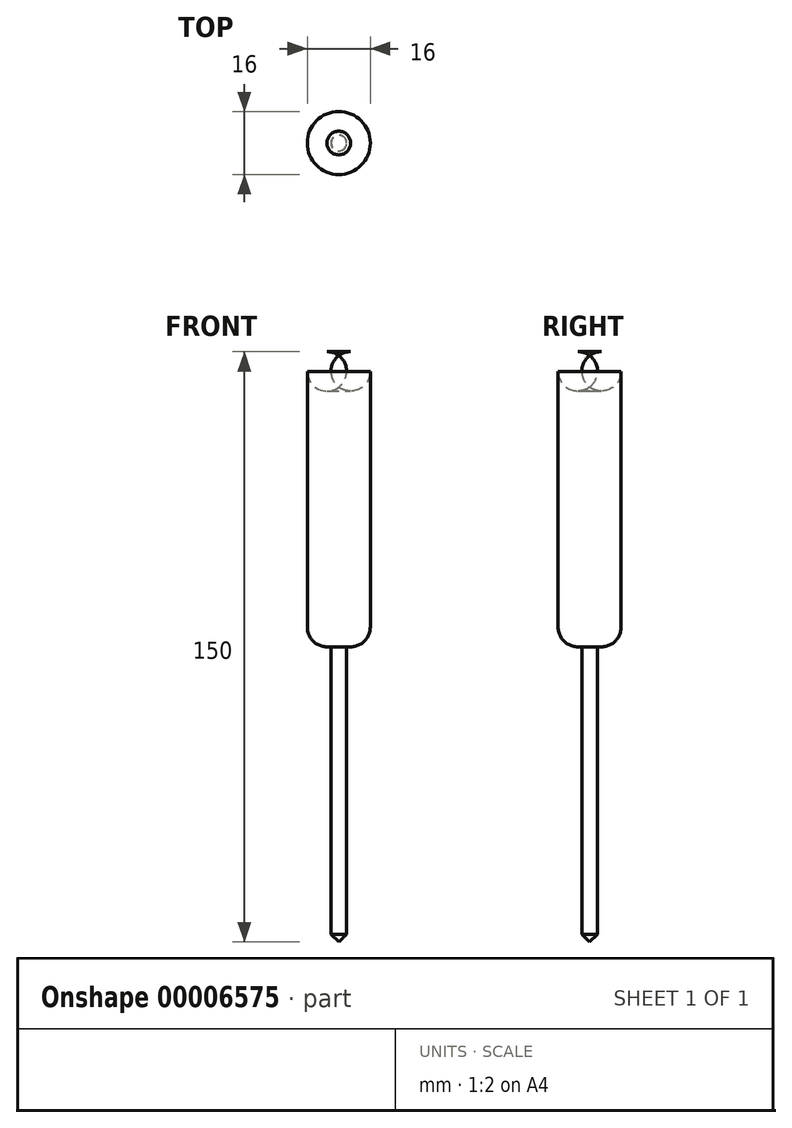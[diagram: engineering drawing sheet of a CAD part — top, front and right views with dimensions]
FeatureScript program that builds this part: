
annotation { "Feature Type Name" : "Feature", "Feature Type Description" : "" }
export const myFeature = defineFeature(function(context is Context, id is Id, definition is map)
    precondition{}
    {
        {
            var Q0;
            Q0=qCreatedBy(makeId("Front.planeOp"),FACE);
            var sketch = newSketch(context, id + "F0", { "sketchPlane" : qUnion([Q0])});
            skLineSegment(sketch, "E0.bottom", {"start": v(-8, 75) * mm, "end": v(0, 75) * mm});
            skLineSegment(sketch, "E0.top", {"start": v(-8, 0) * mm, "end": v(0, 0) * mm});
            skLineSegment(sketch, "E0.left", {"start": v(-8, 75) * mm, "end": v(-8, 0) * mm});
            skLineSegment(sketch, "E0.right", {"start": v(0, 75) * mm, "end": v(0, 0) * mm});
            skLineSegment(sketch, "E1.bottom", {"start": v(0, 0) * mm, "end": v(-2, 0) * mm});
            skLineSegment(sketch, "E1.top", {"start": v(0, -75) * mm, "end": v(-2, -75) * mm});
            skLineSegment(sketch, "E1.left", {"start": v(0, 0) * mm, "end": v(0, -75) * mm});
            skLineSegment(sketch, "E1.right", {"start": v(-2, 0) * mm, "end": v(-2, -75) * mm});
            skSolve(sketch);
        }
        {
            var Q0;
            Q0=qSketchRegion(id+"F0",true);
            var Q1;
            Q1=sQuery(id+"F0.wireOp",EDGE,"E0.right");
            revolve(context, id + "F1", {"entities" : qUnion([Q0]), "axis" : qUnion([Q1]), "revolveType" : RevolveType.FULL});
        }
        {
            var Q0;
            Q0=makeQuery(id+"F1.opRevolve","SWEPT_FACE",FACE,{"disambiguationData":[OSD([sQuery(id+"F0.wireOp",EDGE,"E0.left")])]});
            fillet(context, id + "F2", {"entities" : qUnion([Q0]), "radius" : 5 * mm, "tangentPropagation" : true, "allowEdgeOverflow" : false});
        }
        {
            var Q0;
            Q0=makeQuery(id+"F1.opRevolve","SWEPT_EDGE",EDGE,{"disambiguationData":[OSD([sQuery(id+"F0.wireOp",EDGE,"E1.top"),sQuery(id+"F0.wireOp",EDGE,"E1.right")])]});
            chamfer(context, id + "F3", {"entities" : qUnion([Q0]), "width" : 2 * mm, "tangentPropagation" : true});
        }
    });
